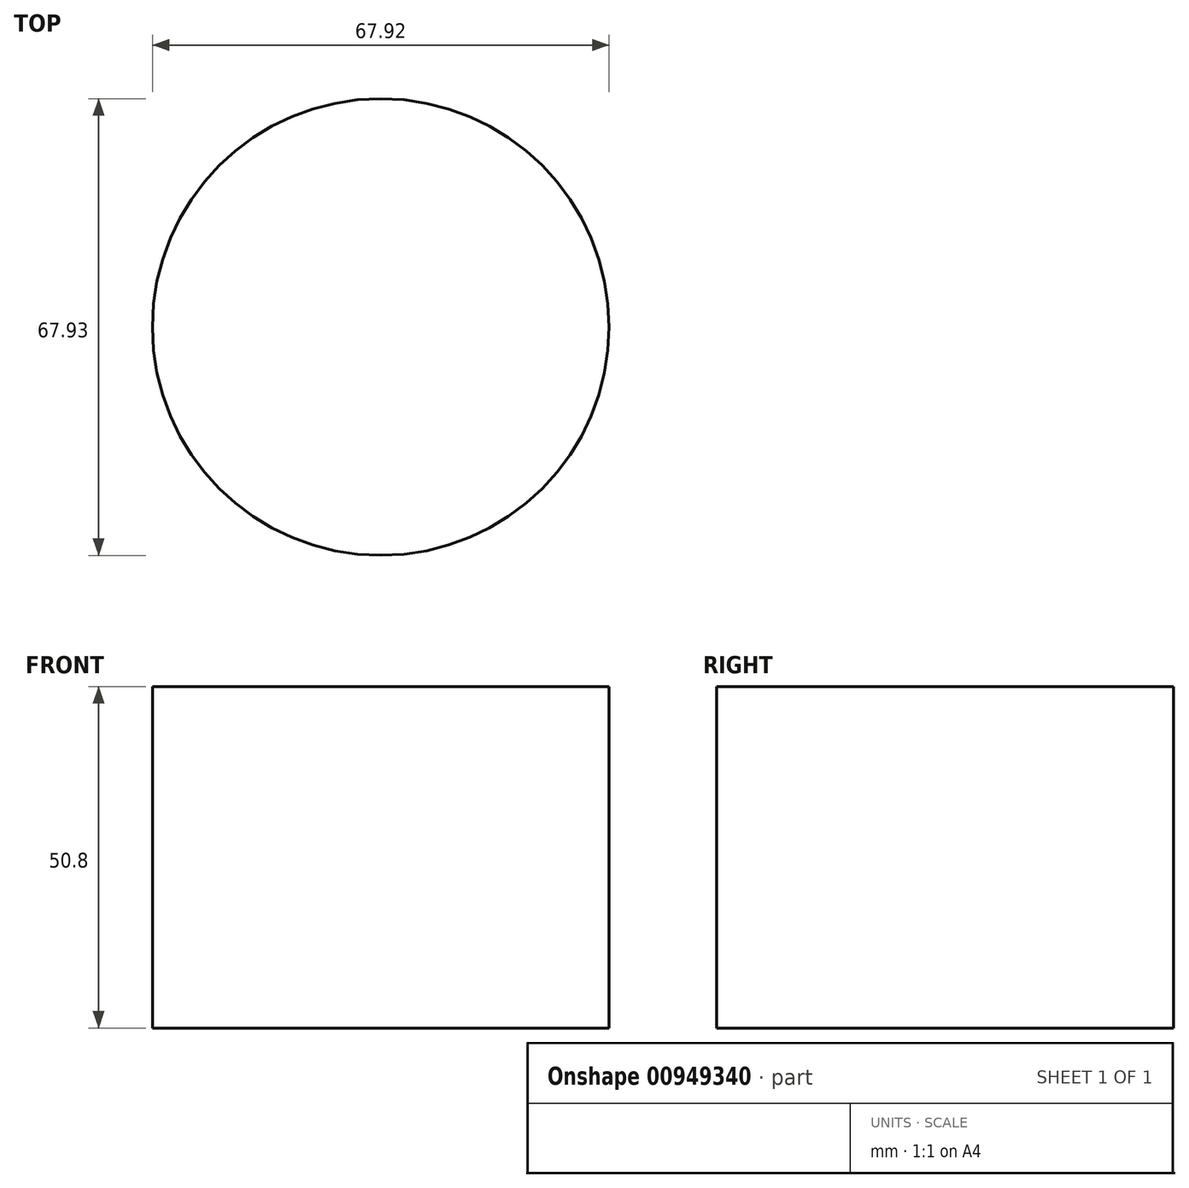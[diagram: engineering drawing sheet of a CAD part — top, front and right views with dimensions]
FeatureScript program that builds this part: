
annotation { "Feature Type Name" : "Feature", "Feature Type Description" : "" }
export const myFeature = defineFeature(function(context is Context, id is Id, definition is map)
    precondition{}
    {
        {
            var Q0;
            Q0=qCreatedBy(makeId("Top.planeOp"),FACE);
            var sketch = newSketch(context, id + "F0", { "sketchPlane" : qUnion([Q0])});
            skCircle(sketch, "E0", {"center": v(15.24, -30.35) * mm, "radius": 33.96 * mm});
            skPoint(sketch, "E0.first.point", {"position": v(0, 0) * mm});
            skPoint(sketch, "E0.second.point", {"position": v(-18.68, -32) * mm});
            skPoint(sketch, "E0.third.point", {"position": v(40.12, -53.48) * mm});
            skCircle(sketch, "E1", {"center": v(15.24, -30.35) * mm, "radius": 22.13 * mm});
            skSolve(sketch);
        }
        {
            var Q0;
            Q0 = qSketchRegion(id + "F0", true);
            var Q1;
            Q1=makeQuery(id+"F0.imprint","IMPRINT",FACE,{"disambiguationData":[TD([[makeQuery(id+"F0.imprint","IMPRINT",EDGE,{"derivedFrom":sQuery(id+"F0.wireOp",EDGE,"E1")}),1.0]])]});
            extrude(context, id + "F1", {"entities" : qUnion([Q0, Q1]), "endBound" : BoundingType.SYMMETRIC, "depth" : 50.8 * mm, "offsetDistance" : 25.4 * mm});
        }
        {
            var Q0;
            Q0 = qBodyType(qCreatedBy(id + "F0" ,EDGE), BodyType.WIRE);
            extrude(context, id + "F2", {"bodyType" : ToolBodyType.SURFACE, "surfaceEntities" : qUnion([Q0]), "endBound" : BoundingType.SYMMETRIC, "depth" : 25.4 * mm, "offsetDistance" : 25.4 * mm});
        }
    });
